# Revit family: 318_9ddfff723c9d4404a56c888b56492b
name_source: partatom
category: Pipe Accessories
units: mm (PartAtom-declared; Revit-internal decimal feet)

## family parameters
Always vertical = Yes
Cut with Voids When Loaded = No
Part Type = Valve - Normal
Round Connector Dimension = Use Diameter
Shared = No
Work Plane-Based = No

## types (1)
- FAR-3611 112
    BP = 15 mm
    CenSd_R_6 = 18 mm
    D1 = 50 mm  [stored 0.164042 ft]
    Description = 1" Brass modular manifold male-female, 2 port 1/2" female
    L = 200 mm  [stored 0.656168 ft]
    L1 = 21 mm  [stored 0.0688976 ft]
    L2 = 3 mm  [stored 0.00984252 ft]
    L3 = 176 mm
    L4 = 13 mm  [stored 0.0426509 ft]
    L5 = 100 mm  [stored 0.328084 ft]
    MP1 = 25 mm
    MP2 = 25 mm
    Manufacturer = FAR
    QmdConnectorList = 301;MP1;302;MP2;303;BP;304;BP
    R = 21 mm  [stored 0.0688976 ft]
    R1 = 13 mm  [stored 0.0426509 ft]
    R3 = 17 mm
    R6 = 9 mm  [stored 0.0295276 ft]
    R8 = 12 mm  [stored 0.0393701 ft]
    URL = www.far.eu
    Z = 31 mm  [stored 0.101706 ft]
    Z__ve = -31 mm  [stored -0.101706 ft]
    magiPartTypeId = 318
    magiProductCode = FAR-3611 112
    magiProductFamilyId = 9ddfff723c9d4404a56c888b56492b
    magiProductId = 9ddfff723c9d4404a56c888b56492b

note: [stored X ft] marks values corroborated as IEEE doubles in the binary element streams (Revit-internal decimal feet)

## geometry (parser evidence)
native form markers: Sweep x2
no freeform markers — native parametric forms only
